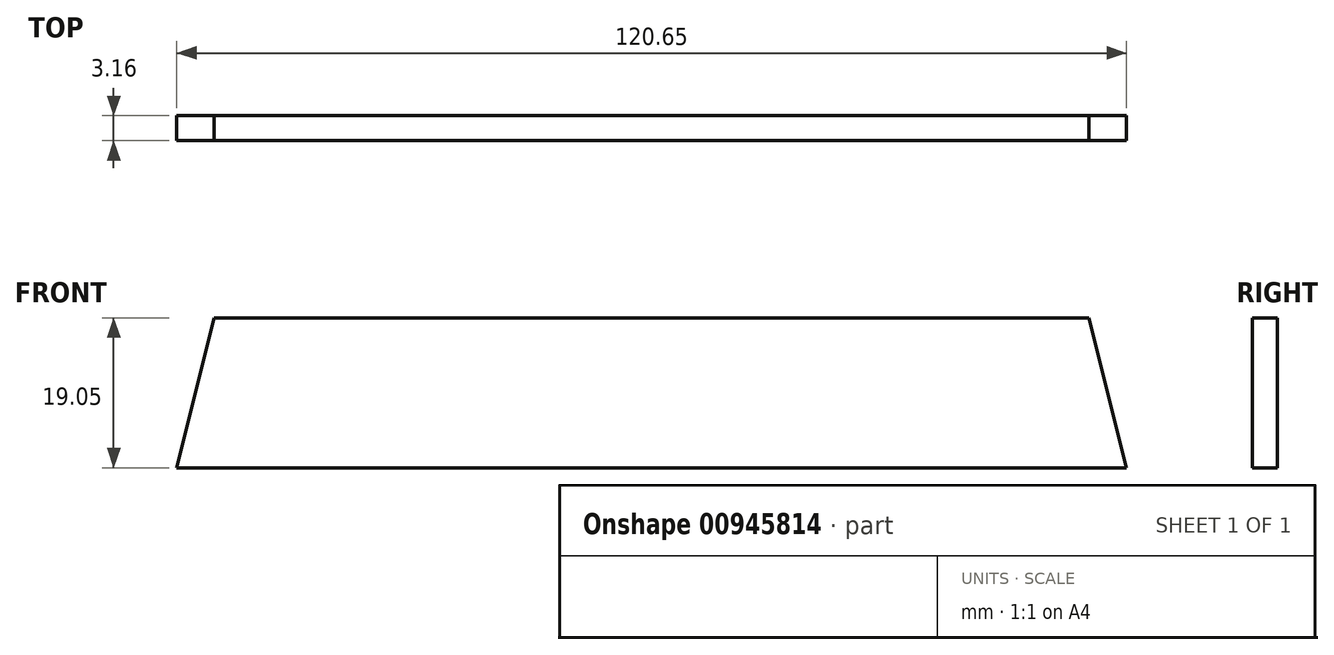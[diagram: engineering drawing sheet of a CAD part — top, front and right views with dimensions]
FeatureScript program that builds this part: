
annotation { "Feature Type Name" : "Feature", "Feature Type Description" : "" }
export const myFeature = defineFeature(function(context is Context, id is Id, definition is map)
    precondition{}
    {
        {
            var Q0;
            Q0=qCreatedBy(makeId("Front.planeOp"),FACE);
            var sketch = newSketch(context, id + "F0", { "sketchPlane" : qUnion([Q0])});
            skLineSegment(sketch, "E0", {"start": v(0, 0) * mm, "end": v(-120.65, 0) * mm});
            skLineSegment(sketch, "E1", {"start": v(0, 0) * mm, "end": v(-4.76, 0) * mm});
            skLineSegment(sketch, "E2", {"start": v(-120.65, 0) * mm, "end": v(-115.89, 0) * mm});
            skLineSegment(sketch, "E3", {"start": v(-4.76, 0) * mm, "end": v(-4.76, 19.05) * mm});
            skLineSegment(sketch, "E4", {"start": v(-4.76, 19.05) * mm, "end": v(0, 0) * mm});
            skLineSegment(sketch, "E5", {"start": v(-4.76, 19.05) * mm, "end": v(-115.89, 19.05) * mm});
            skLineSegment(sketch, "E6", {"start": v(-115.89, 19.05) * mm, "end": v(-115.89, 0) * mm});
            skLineSegment(sketch, "E7", {"start": v(-115.89, 19.05) * mm, "end": v(-120.65, 0) * mm});
            skSolve(sketch);
        }
        {
            var Q0;
            Q0 = qSketchRegion(id + "F0", true);
            extrude(context, id + "F1", {"entities" : qUnion([Q0]), "depth" : 3.16 * mm, "offsetDistance" : 25.4 * mm});
        }
    });
